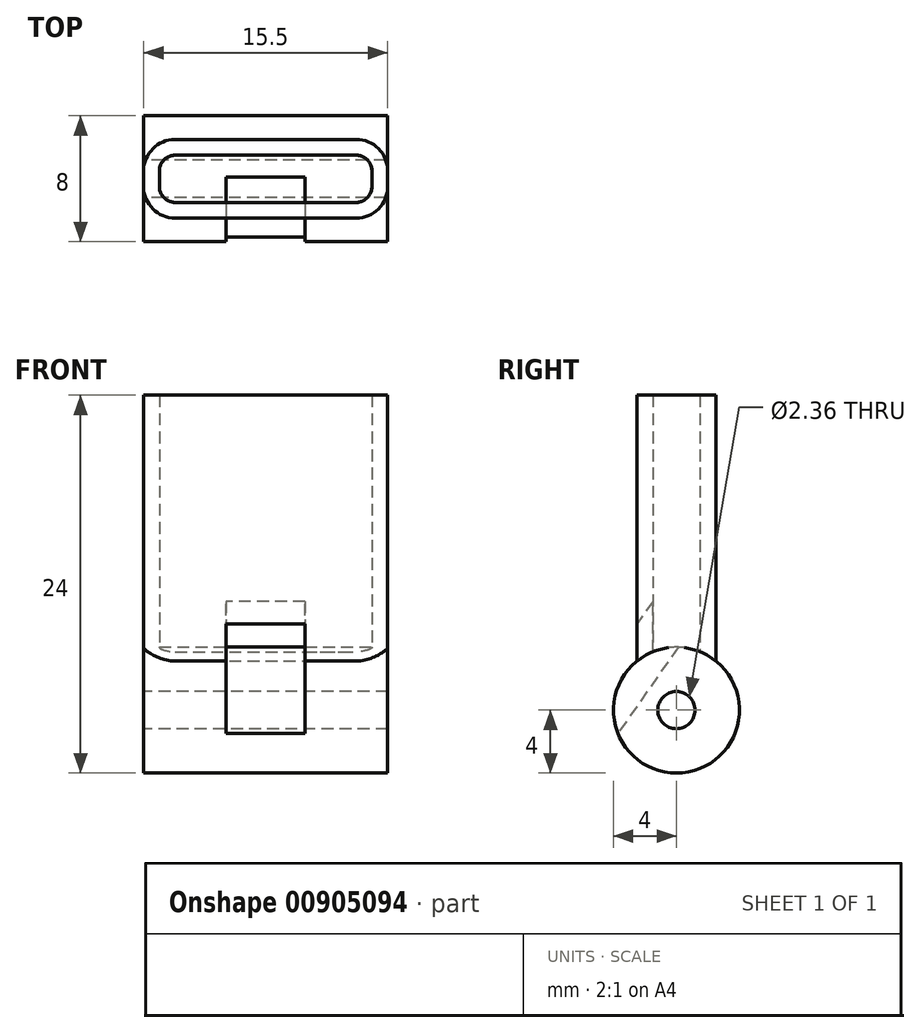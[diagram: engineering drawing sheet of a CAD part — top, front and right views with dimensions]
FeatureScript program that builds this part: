
annotation { "Feature Type Name" : "Feature", "Feature Type Description" : "" }
export const myFeature = defineFeature(function(context is Context, id is Id, definition is map)
    precondition{}
    {
        {
            var Q0;
            Q0=qCreatedBy(makeId("Top.planeOp"),FACE);
            var sketch = newSketch(context, id + "F0", { "sketchPlane" : qUnion([Q0])});
            skLineSegment(sketch, "E0.bottom", {"start": v(-5.75, 1.5) * mm, "end": v(5.75, 1.5) * mm});
            skLineSegment(sketch, "E0.top", {"start": v(-5.75, -1.5) * mm, "end": v(5.75, -1.5) * mm});
            skLineSegment(sketch, "E0.left", {"start": v(-6.75, 0.5) * mm, "end": v(-6.75, -0.5) * mm});
            skLineSegment(sketch, "E0.right", {"start": v(6.75, 0.5) * mm, "end": v(6.75, -0.5) * mm});
            skPoint(sketch, "E0.middle", {"position": v(0, 0) * mm});
            skPoint(sketch, "E1.visualSharp", {"position": v(-6.75, 1.5) * mm});
            skArc(sketch, "E1.filletArc", {"start": v(-5.75, 1.5) * mm, "mid": v(-6.46, 1.2) * mm, "end": v(-6.75, 0.5) * mm});
            skPoint(sketch, "E2.visualSharp", {"position": v(-6.75, -1.5) * mm});
            skArc(sketch, "E2.filletArc", {"start": v(-6.75, -0.5) * mm, "mid": v(-6.46, -1.2) * mm, "end": v(-5.75, -1.5) * mm});
            skPoint(sketch, "E3.visualSharp", {"position": v(6.75, -1.5) * mm});
            skArc(sketch, "E3.filletArc", {"start": v(5.75, -1.5) * mm, "mid": v(6.46, -1.2) * mm, "end": v(6.75, -0.5) * mm});
            skPoint(sketch, "E4.visualSharp", {"position": v(6.75, 1.5) * mm});
            skArc(sketch, "E4.filletArc", {"start": v(6.75, 0.5) * mm, "mid": v(6.46, 1.2) * mm, "end": v(5.75, 1.5) * mm});
            skLineSegment(sketch, "E5.0", {"start": v(-5.75, 2.5) * mm, "end": v(5.75, 2.5) * mm});
            skArc(sketch, "E5.1", {"start": v(7.75, 0.5) * mm, "mid": v(7.16, 1.91) * mm, "end": v(5.75, 2.5) * mm});
            skArc(sketch, "E5.2", {"start": v(-5.75, 2.5) * mm, "mid": v(-7.16, 1.91) * mm, "end": v(-7.75, 0.5) * mm});
            skLineSegment(sketch, "E5.3", {"start": v(7.75, 0.5) * mm, "end": v(7.75, -0.5) * mm});
            skLineSegment(sketch, "E5.4", {"start": v(-7.75, 0.5) * mm, "end": v(-7.75, -0.5) * mm});
            skArc(sketch, "E5.5", {"start": v(-7.75, -0.5) * mm, "mid": v(-7.16, -1.91) * mm, "end": v(-5.75, -2.5) * mm});
            skLineSegment(sketch, "E5.6", {"start": v(-5.75, -2.5) * mm, "end": v(5.75, -2.5) * mm});
            skArc(sketch, "E5.7", {"start": v(5.75, -2.5) * mm, "mid": v(7.16, -1.91) * mm, "end": v(7.75, -0.5) * mm});
            skSolve(sketch);
        }
        {
            var Q0;
            Q0=makeQuery(id+"F0.imprint","IMPRINT",FACE,{"disambiguationData":[TD([[makeQuery(id+"F0.imprint","IMPRINT",EDGE,{"derivedFrom":sQuery(id+"F0.wireOp",EDGE,"E0.bottom")}),1.0]])]});
            extrude(context, id + "F1", {"entities" : qUnion([Q0]), "depth" : 20 * mm, "offsetDistance" : 25 * mm});
        }
        {
            var Q0;
            Q0=makeQuery(id+"F1.opExtrude","SWEPT_FACE",FACE,{"disambiguationData":[OSD([sQuery(id+"F0.wireOp",EDGE,"E5.3")])]});
            var sketch = newSketch(context, id + "F2", { "sketchPlane" : qUnion([Q0])});
            skCircle(sketch, "E6", {"center": v(0, 0) * mm, "radius": 4 * mm});
            skSolve(sketch);
        }
        {
            var Q0;
            {var subQ1=sQuery(id+"F0.wireOp",EDGE,"E5.3");var subQ6=makeQuery(id+"F1.opExtrude","CAP_EDGE",EDGE,{"disambiguationData":[OSD([subQ1])],"isStart":true});Q0=makeQuery(id+"F2.imprint","IMPRINT",FACE,{"disambiguationData":[TD([[makeQuery(id+"F2.imprint","IMPRINT",EDGE,{"derivedFrom":subQ6}),1.0]])]});}
            var Q1;
            {var subQ1=sQuery(id+"F0.wireOp",EDGE,"E5.3");var subQ6=makeQuery(id+"F1.opExtrude","CAP_EDGE",EDGE,{"disambiguationData":[OSD([subQ1])],"isStart":true});Q1=makeQuery(id+"F2.imprint","IMPRINT",FACE,{"disambiguationData":[TD([[makeQuery(id+"F2.imprint","IMPRINT",EDGE,{"derivedFrom":subQ6}),-1.0]])]});}
            extrude(context, id + "F3", {"entities" : qUnion([Q0, Q1]), "operationType" : NewBodyOperationType.ADD, "oppositeDirection" : true, "depth" : 15.5 * mm, "offsetDistance" : 25 * mm});
        }
        {
            var Q0;
            Q0=makeQuery(id+"F3.boolean.opBoolean","INTERSECT",EDGE,{"derivedFrom":[makeQuery(id+"F1.opExtrude","SWEPT_FACE",FACE,{"disambiguationData":[OSD([sQuery(id+"F0.wireOp",EDGE,"E5.6")])]}),makeQuery(id+"F3.opExtrude","SWEPT_FACE",FACE,{"disambiguationData":[OSD([sQuery(id+"F2.wireOp",EDGE,"E6")])]})]});
            cPlane(context, id + "F4", {"entities" : qUnion([Q0]), "cplaneType" : CPlaneType.LINE_ANGLE, "offset" : 25 * mm, "angle" : 55 * degree, "width" : 150 * mm, "height" : 150 * mm});
        }
        {
            var Q0;
            Q0=qCreatedBy(id+"F4.planeOp",FACE);
            var sketch = newSketch(context, id + "F5", { "sketchPlane" : qUnion([Q0])});
            skLineSegment(sketch, "E7.bottom", {"start": v(-2.5, -5.2) * mm, "end": v(2.5, -5.2) * mm});
            skLineSegment(sketch, "E7.top", {"start": v(-2.5, -2.2) * mm, "end": v(2.5, -2.2) * mm});
            skLineSegment(sketch, "E7.left", {"start": v(-2.5, -5.2) * mm, "end": v(-2.5, -2.2) * mm});
            skLineSegment(sketch, "E7.right", {"start": v(2.5, -5.2) * mm, "end": v(2.5, -2.2) * mm});
            skPoint(sketch, "E7.middle", {"position": v(0, -3.7) * mm});
            skSolve(sketch);
        }
        {
            var Q0;
            Q0 = qSketchRegion(id + "F5", true);
            extrude(context, id + "F6", {"entities" : qUnion([Q0]), "operationType" : NewBodyOperationType.REMOVE, "depth" : 9 * mm, "offsetDistance" : 25 * mm, "symmetric" : true});
        }
        {
            var Q0;
            Q0=makeQuery(id+"F3.boolean.opBoolean","MERGE",FACE,{"derivedFrom":[makeQuery(id+"F1.opExtrude","SWEPT_FACE",FACE,{"disambiguationData":[OSD([sQuery(id+"F0.wireOp",EDGE,"E5.4")])]}),makeQuery(id+"F3.opExtrude","CAP_FACE",FACE,{"disambiguationData":[OSD([sQuery(id+"F2.wireOp",EDGE,"E6")])],"isStart":false})]});
            var sketch = newSketch(context, id + "F7", { "sketchPlane" : qUnion([Q0])});
            skCircle(sketch, "E8", {"center": v(0, 0) * mm, "radius": 1.18 * mm});
            skSolve(sketch);
        }
        {
            var Q0;
            Q0 = qSketchRegion(id + "F7", true);
            extrude(context, id + "F8", {"entities" : qUnion([Q0]), "operationType" : NewBodyOperationType.REMOVE, "oppositeDirection" : true, "depth" : 25 * mm, "offsetDistance" : 25 * mm});
        }
    });
